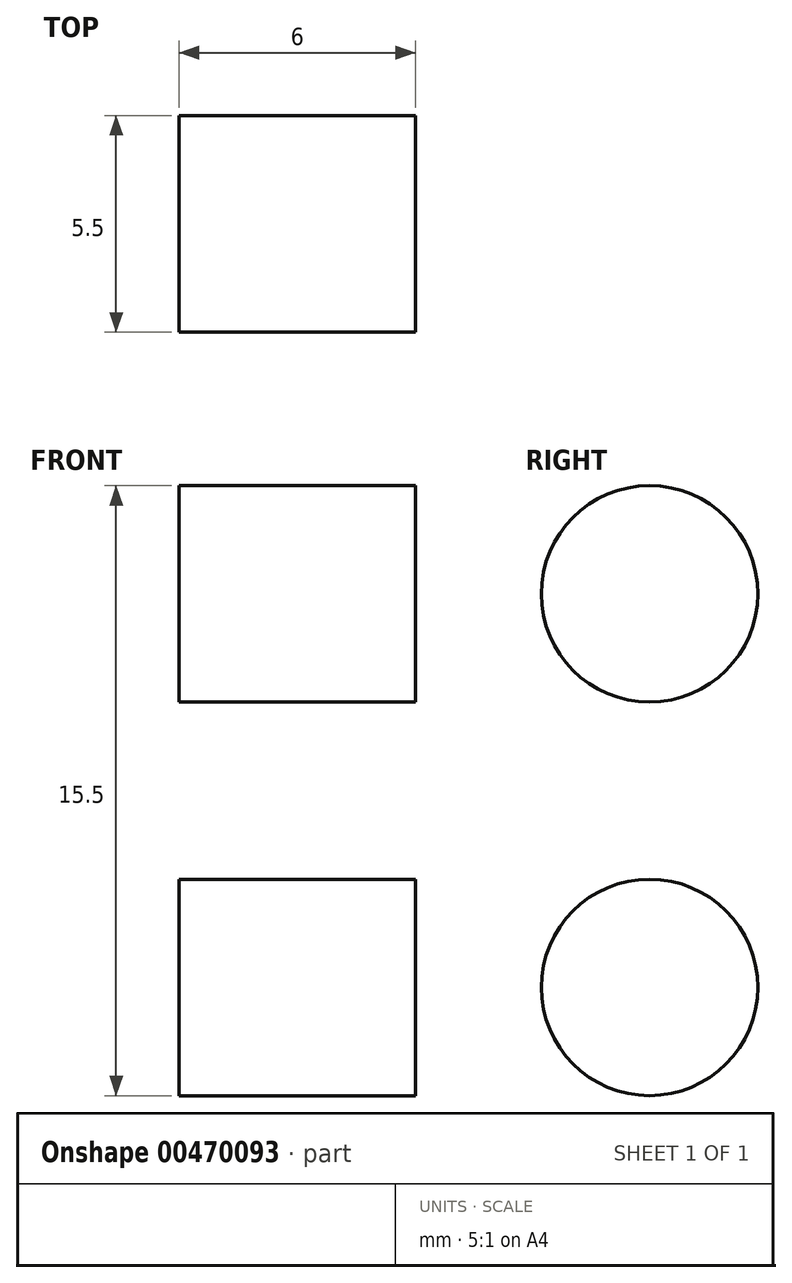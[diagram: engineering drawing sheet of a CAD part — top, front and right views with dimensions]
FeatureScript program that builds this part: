
annotation { "Feature Type Name" : "Feature", "Feature Type Description" : "" }
export const myFeature = defineFeature(function(context is Context, id is Id, definition is map)
    precondition{}
    {
        {
            var Q0;
            Q0=qCreatedBy(makeId("Top.planeOp"),FACE);
            var sketch = newSketch(context, id + "F0", { "sketchPlane" : qUnion([Q0])});
            skLineSegment(sketch, "E0.bottom", {"start": v(0, 0) * mm, "end": v(6, 0) * mm});
            skLineSegment(sketch, "E0.top", {"start": v(0, -120) * mm, "end": v(6, -120) * mm});
            skLineSegment(sketch, "E0.left", {"start": v(0, 0) * mm, "end": v(0, -120) * mm});
            skLineSegment(sketch, "E0.right", {"start": v(6, 0) * mm, "end": v(6, -120) * mm});
            skSolve(sketch);
        }
        {
            var Q0;
            Q0=makeQuery(id+"F0.imprint","IMPRINT",FACE,{"disambiguationData":[TD([[makeQuery(id+"F0.imprint","IMPRINT",EDGE,{"derivedFrom":sQuery(id+"F0.wireOp",EDGE,"E0.bottom")}),-1.0]])]});
            extrude(context, id + "F1", {"entities" : qUnion([Q0]), "depth" : 20 * mm});
        }
        {
            var Q0;
            Q0=makeQuery(id+"F1.opExtrude","CAP_FACE",FACE,{"disambiguationData":[OSD([sQuery(id+"F0.wireOp",EDGE,"E0.bottom"),sQuery(id+"F0.wireOp",EDGE,"E0.top"),sQuery(id+"F0.wireOp",EDGE,"E0.left"),sQuery(id+"F0.wireOp",EDGE,"E0.right")])],"isStart":false});
            var sketch = newSketch(context, id + "F2", { "sketchPlane" : qUnion([Q0])});
            skCircle(sketch, "E1", {"center": v(3, -14) * mm, "radius": 2.1 * mm});
            skCircle(sketch, "E2", {"center": v(3, -106) * mm, "radius": 2.1 * mm});
            skLineSegment(sketch, "E3", {"start": v(3, -14) * mm, "end": v(3, -106) * mm, "construction": true});
            skLineSegment(sketch, "E4", {"start": v(0, -60) * mm, "end": v(6, -60) * mm, "construction": true});
            skPoint(sketch, "E5", {"position": v(3, -60) * mm});
            skCircle(sketch, "E6", {"center": v(3, -60) * mm, "radius": 2.1 * mm});
            skSolve(sketch);
        }
        {
            var Q0;
            Q0=makeQuery(id+"F2.imprint","IMPRINT",FACE,{"disambiguationData":[TD([[makeQuery(id+"F2.imprint","IMPRINT",EDGE,{"derivedFrom":sQuery(id+"F2.wireOp",EDGE,"E1")}),1.0]])]});
            var Q1;
            Q1=makeQuery(id+"F2.imprint","IMPRINT",FACE,{"disambiguationData":[TD([[makeQuery(id+"F2.imprint","IMPRINT",EDGE,{"derivedFrom":sQuery(id+"F2.wireOp",EDGE,"E2")}),1.0]])]});
            var Q2;
            Q2=makeQuery(id+"F2.imprint","IMPRINT",FACE,{"disambiguationData":[TD([[makeQuery(id+"F2.imprint","IMPRINT",EDGE,{"derivedFrom":sQuery(id+"F2.wireOp",EDGE,"E6")}),1.0]])]});
            extrude(context, id + "F3", {"entities" : qUnion([Q0, Q1, Q2]), "operationType" : NewBodyOperationType.REMOVE, "oppositeDirection" : true, "depth" : 20 * mm});
        }
        {
            var Q0;
            Q0=makeQuery(id+"F1.opExtrude","SWEPT_FACE",FACE,{"disambiguationData":[OSD([sQuery(id+"F0.wireOp",EDGE,"E0.right")])]});
            var sketch = newSketch(context, id + "F4", { "sketchPlane" : qUnion([Q0])});
            skCircle(sketch, "E7", {"center": v(-5, 15) * mm, "radius": 2.75 * mm});
            skCircle(sketch, "E8", {"center": v(-5, 5) * mm, "radius": 2.75 * mm});
            skLineSegment(sketch, "E9", {"start": v(-60, 0) * mm, "end": v(-60, 20) * mm, "construction": true});
            skCircle(sketch, "E10.MirrorC", {"center": v(-115, 15) * mm, "radius": 2.75 * mm});
            skCircle(sketch, "E11.MirrorC", {"center": v(-115, 5) * mm, "radius": 2.75 * mm});
            skSolve(sketch);
        }
        {
            var Q0;
            Q0=makeQuery(id+"F4.imprint","IMPRINT",FACE,{"disambiguationData":[TD([[makeQuery(id+"F4.imprint","IMPRINT",EDGE,{"derivedFrom":sQuery(id+"F4.wireOp",EDGE,"E10.MirrorC")}),-1.0]])]});
            var Q1;
            Q1=makeQuery(id+"F4.imprint","IMPRINT",FACE,{"disambiguationData":[TD([[makeQuery(id+"F4.imprint","IMPRINT",EDGE,{"derivedFrom":sQuery(id+"F4.wireOp",EDGE,"E11.MirrorC")}),-1.0]])]});
            var Q2;
            Q2=makeQuery(id+"F4.imprint","IMPRINT",FACE,{"disambiguationData":[TD([[makeQuery(id+"F4.imprint","IMPRINT",EDGE,{"derivedFrom":sQuery(id+"F4.wireOp",EDGE,"E8")}),1.0]])]});
            var Q3;
            Q3=makeQuery(id+"F4.imprint","IMPRINT",FACE,{"disambiguationData":[TD([[makeQuery(id+"F4.imprint","IMPRINT",EDGE,{"derivedFrom":sQuery(id+"F4.wireOp",EDGE,"E7")}),1.0]])]});
            extrude(context, id + "F5", {"entities" : qUnion([Q0, Q1, Q2, Q3]), "operationType" : NewBodyOperationType.REMOVE, "oppositeDirection" : true, "depth" : 25 * mm});
        }
    });
